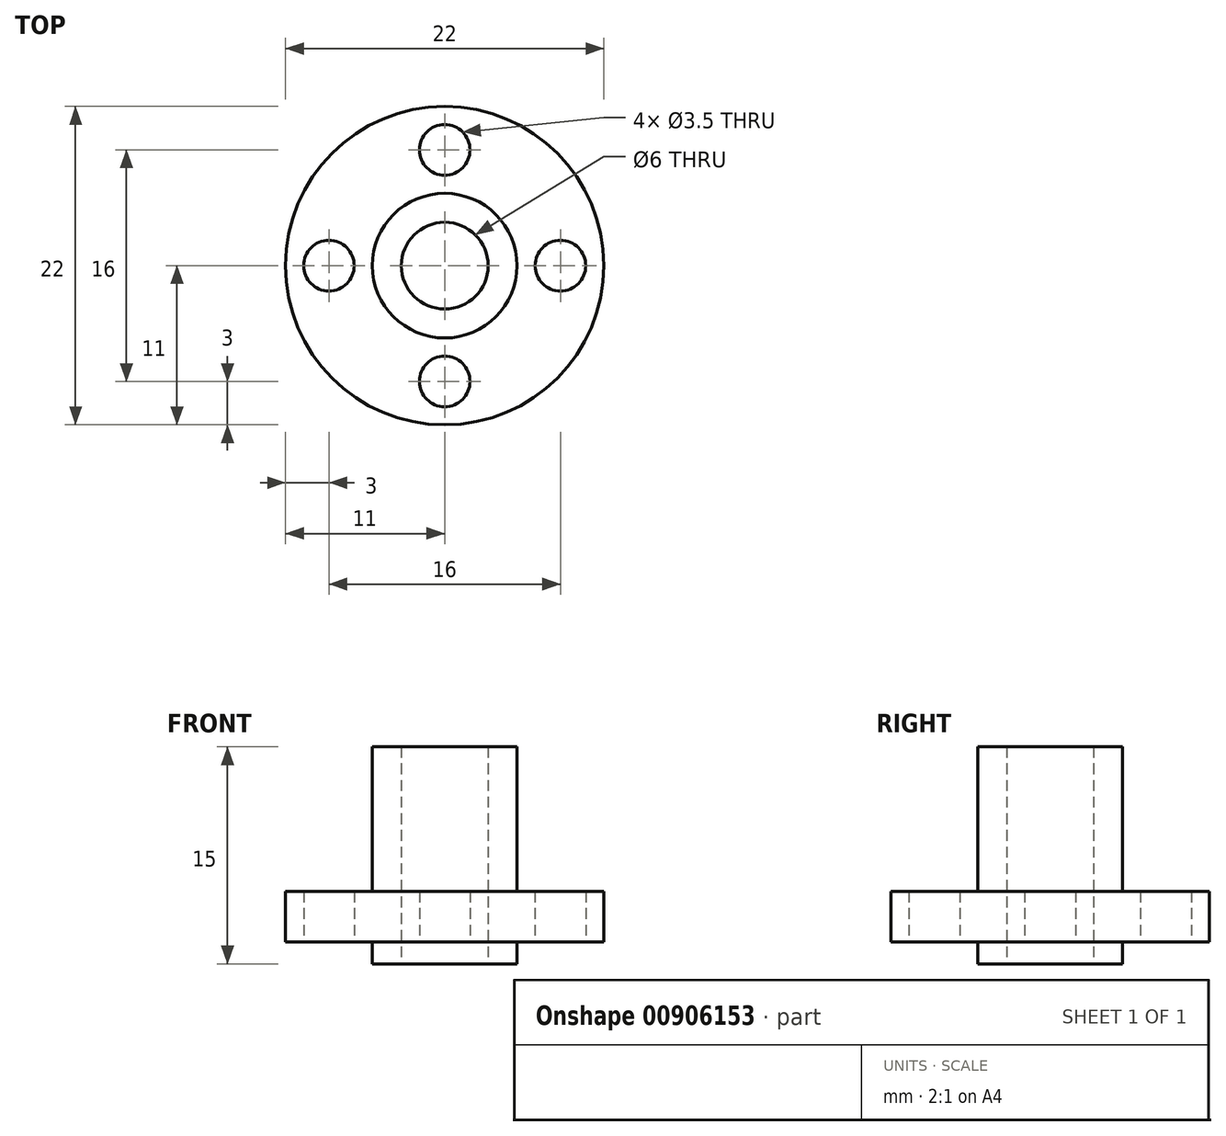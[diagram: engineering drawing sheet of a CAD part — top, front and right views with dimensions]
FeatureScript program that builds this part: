
annotation { "Feature Type Name" : "Feature", "Feature Type Description" : "" }
export const myFeature = defineFeature(function(context is Context, id is Id, definition is map)
    precondition{}
    {
        {
            var Q0;
            Q0=qCreatedBy(makeId("Top.planeOp"),FACE);
            var sketch = newSketch(context, id + "F0", { "sketchPlane" : qUnion([Q0])});
            skCircle(sketch, "E0", {"center": v(0, 0) * mm, "radius": 11 * mm});
            skCircle(sketch, "E1", {"center": v(0, 0) * mm, "radius": 4 * mm});
            skSolve(sketch);
        }
        {
            var Q0;
            Q0 = qSketchRegion(id + "F0", true);
            extrude(context, id + "F1", {"entities" : qUnion([Q0]), "depth" : 3.5 * mm, "offsetDistance" : 25 * mm});
        }
        {
            var Q0;
            Q0=makeQuery(id+"F1.opExtrude","CAP_FACE",FACE,{"disambiguationData":[OSD([sQuery(id+"F0.wireOp",EDGE,"E0")])],"isStart":false});
            var sketch = newSketch(context, id + "F2", { "sketchPlane" : qUnion([Q0])});
            skCircle(sketch, "E2", {"center": v(0, 0) * mm, "radius": 5 * mm});
            skCircle(sketch, "E3", {"center": v(0, 0) * mm, "radius": 3 * mm});
            skSolve(sketch);
        }
        {
            var Q0;
            Q0 = qSketchRegion(id + "F2", true);
            extrude(context, id + "F3", {"entities" : qUnion([Q0]), "operationType" : NewBodyOperationType.ADD, "depth" : 10 * mm, "offsetDistance" : 25 * mm});
        }
        {
            var Q0;
            Q0 = qSketchRegion(id + "F2", true);
            extrude(context, id + "F4", {"entities" : qUnion([Q0]), "operationType" : NewBodyOperationType.ADD, "oppositeDirection" : true, "depth" : 5 * mm, "offsetDistance" : 25 * mm});
        }
        {
            var Q0;
            Q0=makeQuery(id+"F1.opExtrude","CAP_FACE",FACE,{"disambiguationData":[OSD([sQuery(id+"F0.wireOp",EDGE,"E0"),sQuery(id+"F0.wireOp",EDGE,"E1")])],"isStart":true});
            var sketch = newSketch(context, id + "F5", { "sketchPlane" : qUnion([Q0])});
            skCircle(sketch, "E4", {"center": v(0, 0) * mm, "radius": 8 * mm, "construction": true});
            skCircle(sketch, "E5", {"center": v(-8, 0) * mm, "radius": 1.75 * mm});
            skCircle(sketch, "E6", {"center": v(0, 8) * mm, "radius": 1.75 * mm});
            skCircle(sketch, "E7", {"center": v(8, 0) * mm, "radius": 1.75 * mm});
            skCircle(sketch, "E8", {"center": v(0, -8) * mm, "radius": 1.75 * mm});
            skSolve(sketch);
        }
        {
            var Q0;
            Q0 = qSketchRegion(id + "F5", true);
            extrude(context, id + "F6", {"entities" : qUnion([Q0]), "operationType" : NewBodyOperationType.REMOVE, "oppositeDirection" : true, "depth" : 25 * mm, "offsetDistance" : 25 * mm});
        }
    });
